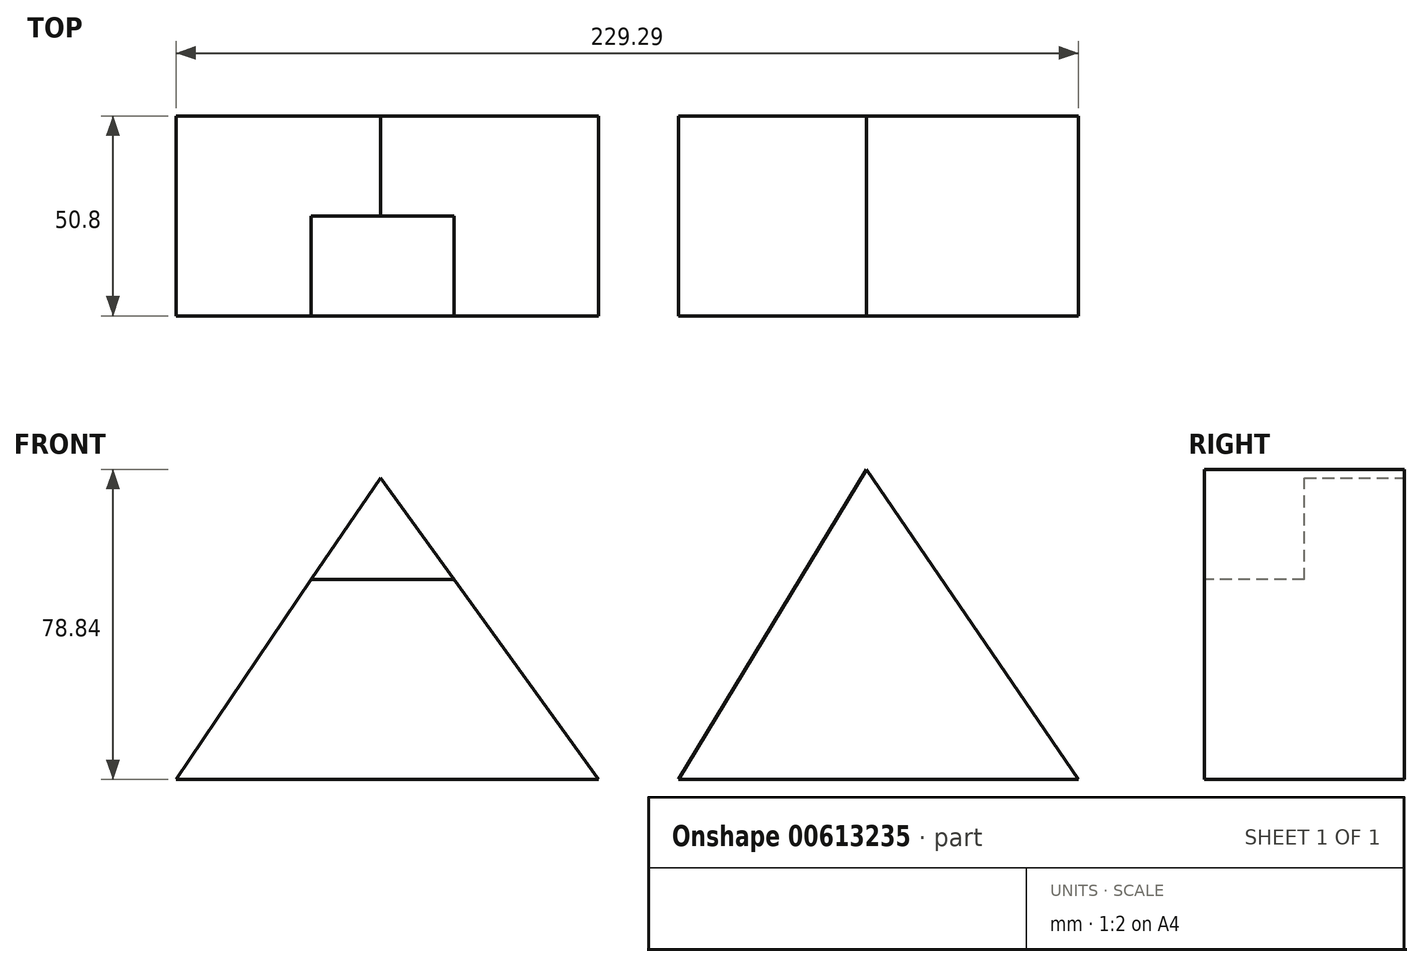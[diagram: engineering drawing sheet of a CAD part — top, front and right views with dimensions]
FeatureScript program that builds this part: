
annotation { "Feature Type Name" : "Feature", "Feature Type Description" : "" }
export const myFeature = defineFeature(function(context is Context, id is Id, definition is map)
    precondition{}
    {
        {
            var Q0;
            Q0=qCreatedBy(makeId("Front.planeOp"),FACE);
            var sketch = newSketch(context, id + "F0", { "sketchPlane" : qUnion([Q0])});
            skLineSegment(sketch, "E0", {"start": v(0, 0) * mm, "end": v(51.94, 76.7) * mm});
            skLineSegment(sketch, "E1", {"start": v(51.94, 76.7) * mm, "end": v(107.4, 0) * mm});
            skLineSegment(sketch, "E2", {"start": v(107.4, 0) * mm, "end": v(0, 0) * mm});
            skSolve(sketch);
        }
        {
            var Q0;
            Q0 = qSketchRegion(id + "F0", true);
            extrude(context, id + "F1", {"entities" : qUnion([Q0]), "depth" : 50.8 * mm, "offsetDistance" : 25.4 * mm});
        }
        {
            var Q0;
            Q0=makeQuery(id+"F1.opExtrude","CAP_FACE",FACE,{"disambiguationData":[OSD([sQuery(id+"F0.wireOp",EDGE,"E0"),sQuery(id+"F0.wireOp",EDGE,"E1"),sQuery(id+"F0.wireOp",EDGE,"E2")])],"isStart":false});
            var sketch = newSketch(context, id + "F2", { "sketchPlane" : qUnion([Q0])});
            skLineSegment(sketch, "E3", {"start": v(34.4, 50.8) * mm, "end": v(70.67, 50.8) * mm});
            skSolve(sketch);
        }
        {
            var Q0;
            Q0 = qSketchRegion(id + "F2", true);
            var Q1;
            {var subQ0=sQuery(id+"F2.wireOp",EDGE,"E3");Q1=makeQuery(id+"F2.imprint","IMPRINT",FACE,{"disambiguationData":[TD([[makeQuery(id+"F2.imprint","IMPRINT",EDGE,{"derivedFrom":subQ0}),1.0]])]});}
            extrude(context, id + "F3", {"entities" : qUnion([Q0, Q1]), "operationType" : NewBodyOperationType.REMOVE, "oppositeDirection" : true, "depth" : 25.4 * mm, "offsetDistance" : 25.4 * mm});
        }
        {
            var Q0;
            Q0=qCreatedBy(makeId("Front.planeOp"),FACE);
            var sketch = newSketch(context, id + "F4", { "sketchPlane" : qUnion([Q0])});
            skLineSegment(sketch, "E4", {"start": v(127.69, 0) * mm, "end": v(229.29, 0) * mm});
            skLineSegment(sketch, "E5", {"start": v(127.69, 0) * mm, "end": v(175.4, 78.84) * mm});
            skLineSegment(sketch, "E6", {"start": v(175.4, 78.84) * mm, "end": v(229.29, 0) * mm});
            skSolve(sketch);
        }
        {
            var Q0;
            Q0 = qSketchRegion(id + "F4", true);
            extrude(context, id + "F5", {"entities" : qUnion([Q0]), "depth" : 50.8 * mm, "offsetDistance" : 25.4 * mm});
        }
    });
